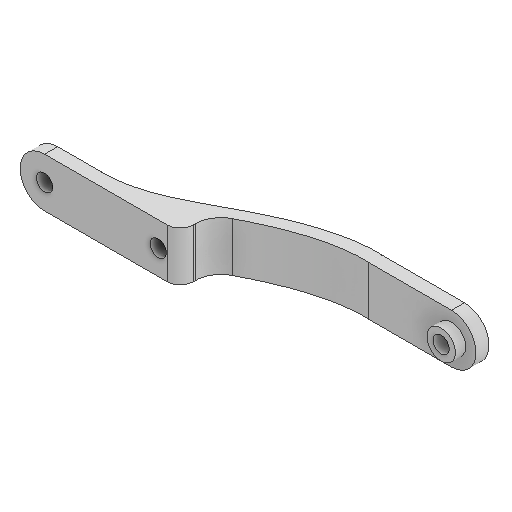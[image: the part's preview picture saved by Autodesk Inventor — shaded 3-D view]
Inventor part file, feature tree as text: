
AUTODESK INVENTOR PART (.ipt)
format: ipt  version: 2025 (Build 290162000, 162)  size: 210,944 bytes
history: native  units: in
note: dims shown in document units (in); Inventor stores cm internally (conversion verified against a paired STEP export)
features: sketch x9, extrude x7, plane x3, projected_geometry x3, fillet x2, sweep x1
ambient origin geometry x8: Origin, YZ Plane, XZ Plane, XY Plane, X Axis, Y Axis, Z Axis, Center Point
bodies: Solid1 (feature_tree)
feature tree (25):
  extrude  "Extrusion1"  Depth=0.315in
  extrude  "Extrusion2"  Depth=0.25in TaperAngle=0.0deg
  plane  "Work Plane1"
  extrude  "Extrusion3"  Depth=0.1969in TaperAngle=0.0deg
  extrude  "Extrusion4"  Depth=0.25in TaperAngle=0.0deg
  plane  "Work Plane2"
  sweep  "Sweep1"
  extrude  "Extrusion5"  Depth=1.0in TaperAngle=0.0deg
  extrude  "Extrusion6"  Depth=0.5in
  plane  "Work Plane3"
  extrude  "Extrusion7"  Depth=0.25in TaperAngle=0.0deg
  fillet  "Fillet1"  Radius=0.5in
  fillet  "Fillet2"  Radius=0.25in
  sketch  "Sketch1"  dims[d0=6.5in d1=0.315in]
  sketch  "Sketch2"  dims[d2=0.315in d3=0.25in d4=0.0in]
  sketch  "Sketch3"  dims[d5=0.5512in d6=0.1969in d7=0.0in]
  projected_geometry  "Projected Loop1"
  sketch  "Sketch4"  dims[d8=1.31in d9=0.25in d10=0.0in]
  sketch  "Sketch5"  dims[d11=0.3937in d12=0.0in d13=0.0in d14=0.0in]
  sketch  "Sketch6"  dims[d15=0.0in d16=0.0in d17=1.0in d18=0.0in]
  projected_geometry  "Projected Loop2"
  sketch  "Sketch7"  dims[d19=-0.5in d20=0.5in]
  projected_geometry  "Projected Loop3"
  sketch  "Sketch8"  dims[d21=0.315in d22=1.0in d23=0.0in d24=0.5in d25=0.25in]
  sketch  "Sketch9"
